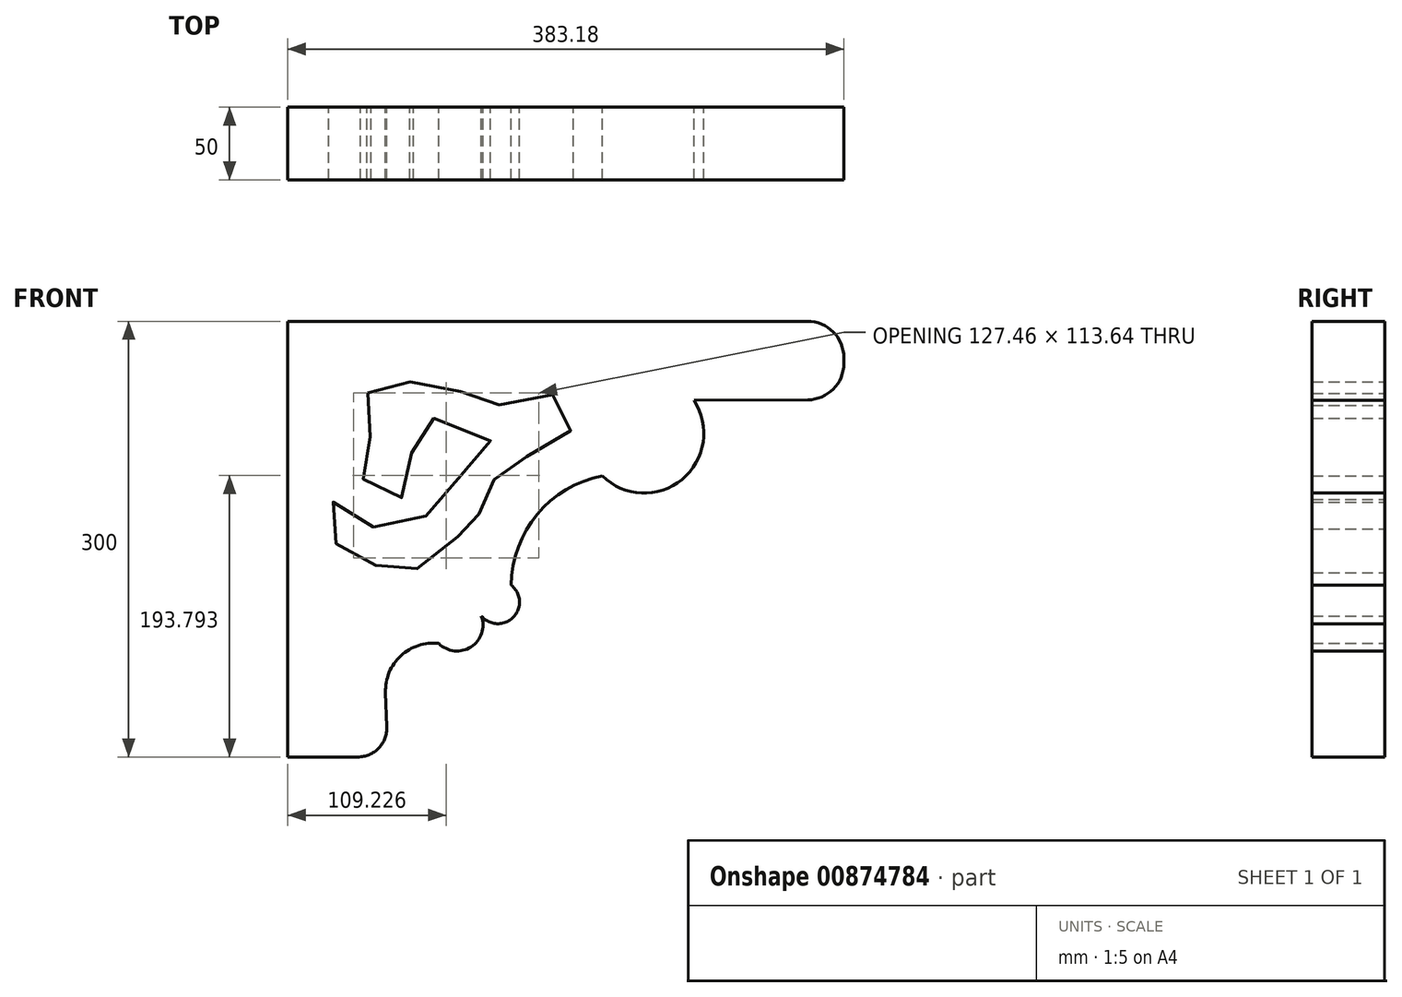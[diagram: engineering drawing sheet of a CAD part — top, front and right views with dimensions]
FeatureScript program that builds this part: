
annotation { "Feature Type Name" : "Feature", "Feature Type Description" : "" }
export const myFeature = defineFeature(function(context is Context, id is Id, definition is map)
    precondition{}
    {
        {
            var Q0;
            Q0=qCreatedBy(makeId("Front.planeOp"),FACE);
            var sketch = newSketch(context, id + "F0", { "sketchPlane" : qUnion([Q0])});
            skLineSegment(sketch, "E0.bottom", {"start": v(-274.86, 221.83) * mm, "end": v(83.32, 221.83) * mm});
            skLineSegment(sketch, "E0.top", {"start": v(-274.86, -78.17) * mm, "end": v(-226.54, -78.17) * mm});
            skLineSegment(sketch, "E0.left", {"start": v(-274.86, 221.83) * mm, "end": v(-274.86, -78.17) * mm});
            skLineSegment(sketch, "E0.right", {"start": v(108.32, 196.83) * mm, "end": v(108.32, 192.75) * mm});
            skArc(sketch, "E1", {"start": v(-58.16, 115.4) * mm, "mid": v(-3.2, 112.94) * mm, "end": v(5.03, 167.34) * mm});
            skPoint(sketch, "E1.startSnap0", {"position": v(-58.16, 118.43) * mm});
            skArc(sketch, "E2", {"start": v(-58.16, 115.4) * mm, "mid": v(-102.9, 88.9) * mm, "end": v(-120.82, 40.1) * mm});
            skArc(sketch, "E3", {"start": v(-144.12, 23.72) * mm, "mid": v(-121.5, 16.3) * mm, "end": v(-120.82, 40.1) * mm});
            skArc(sketch, "E4", {"start": v(-170.8, 0) * mm, "mid": v(-146.28, -0.72) * mm, "end": v(-144.12, 23.72) * mm});
            skLineSegment(sketch, "E5", {"start": v(5.03, 167.34) * mm, "end": v(83.45, 167.75) * mm});
            skLineSegment(sketch, "E6", {"start": v(-207.45, -33.85) * mm, "end": v(-206.56, -57.4) * mm});
            skArc(sketch, "E7", {"start": v(-170.8, 0) * mm, "mid": v(-196.92, -8.48) * mm, "end": v(-207.45, -33.85) * mm});
            skPoint(sketch, "E8.visualSharp", {"position": v(108.32, 221.83) * mm});
            skArc(sketch, "E8.filletArc", {"start": v(108.32, 196.83) * mm, "mid": v(101, 214.5) * mm, "end": v(83.32, 221.83) * mm});
            skPoint(sketch, "E9.visualSharp", {"position": v(108.32, 167.88) * mm});
            skArc(sketch, "E9.filletArc", {"start": v(83.45, 167.75) * mm, "mid": v(101.05, 175.12) * mm, "end": v(108.32, 192.75) * mm});
            skPoint(sketch, "E10.visualSharp", {"position": v(-205.76, -78.17) * mm});
            skArc(sketch, "E10.filletArc", {"start": v(-226.54, -78.17) * mm, "mid": v(-212.13, -72.04) * mm, "end": v(-206.56, -57.4) * mm});
            skFitSpline(sketch, "E11", {"points": [v(-219.58, 172.44) * mm, v(-193.84, 180.07) * mm, v(-155.72, 173.4) * mm, v(-133.8, 163.87) * mm, v(-92.8, 171.5) * mm, v(-78.51, 149.58) * mm, v(-108.06, 129.57) * mm, v(-129.03, 116.23) * mm, v(-140.47, 100.03) * mm, v(-146.18, 80.97) * mm, v(-159.53, 72.4) * mm, v(-190.03, 49.53) * mm, v(-215.76, 54.3) * mm, v(-241.5, 68.59) * mm, v(-244.36, 97.17) * mm, v(-220.53, 81.93) * mm, v(-179.54, 87.64) * mm, v(-155.72, 115.28) * mm, v(-135.7, 141) * mm, v(-186.22, 152.43) * mm, v(-188.12, 117.18) * mm, v(-201.47, 99.08) * mm, v(-224.34, 117.18) * mm, v(-217.67, 144.81) * mm, v(-219.58, 172.44) * mm]});
            skSolve(sketch);
        }
        {
            var Q0;
            Q0 = qSketchRegion(id + "F0", true);
            extrude(context, id + "F1", {"entities" : qUnion([Q0]), "depth" : 50 * mm, "offsetDistance" : 25 * mm});
        }
    });
